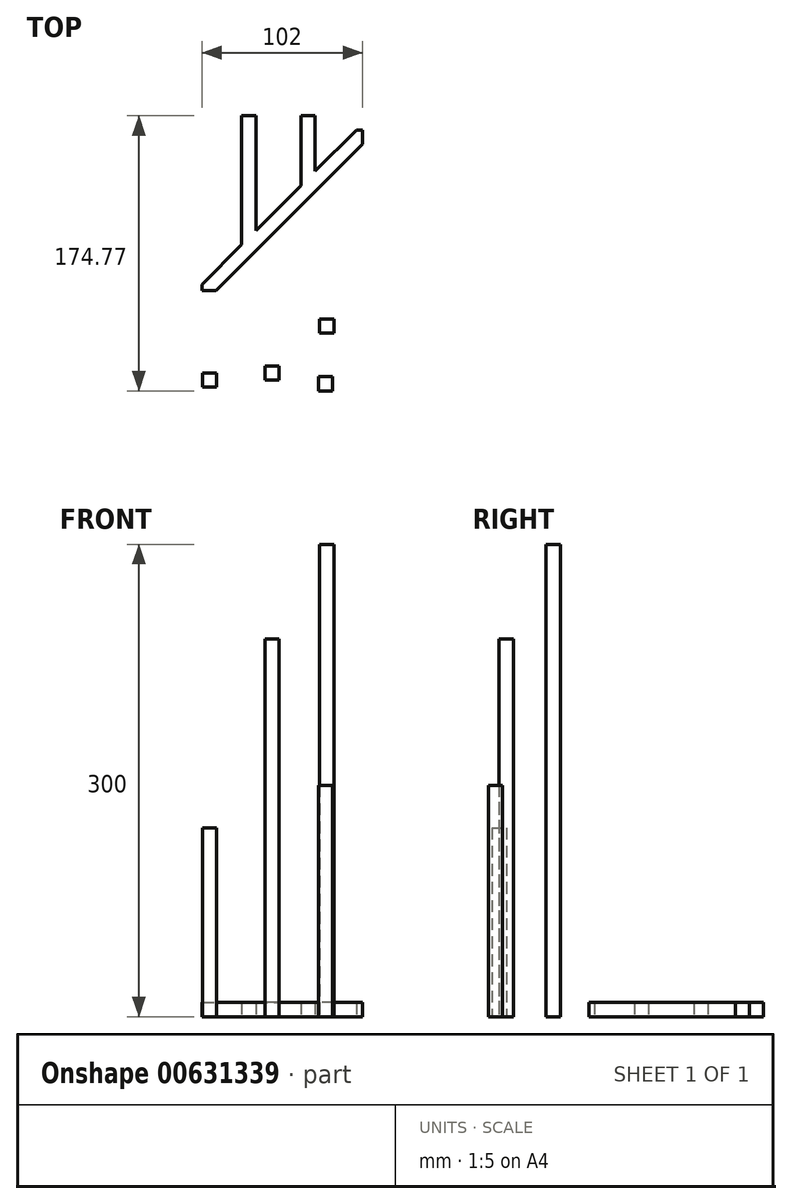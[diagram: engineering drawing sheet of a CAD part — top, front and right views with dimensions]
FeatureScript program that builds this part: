
annotation { "Feature Type Name" : "Feature", "Feature Type Description" : "" }
export const myFeature = defineFeature(function(context is Context, id is Id, definition is map)
    precondition{}
    {
        {
            var Q0;
            Q0=qCreatedBy(makeId("Top.planeOp"),FACE);
            var sketch = newSketch(context, id + "F0", { "sketchPlane" : qUnion([Q0])});
            skLineSegment(sketch, "E0.bottom", {"start": v(4.5, -4.5) * mm, "end": v(-4.5, -4.5) * mm});
            skLineSegment(sketch, "E0.top", {"start": v(4.5, 4.5) * mm, "end": v(-4.5, 4.5) * mm});
            skLineSegment(sketch, "E0.left", {"start": v(4.5, -4.5) * mm, "end": v(4.5, 4.5) * mm});
            skLineSegment(sketch, "E0.right", {"start": v(-4.5, -4.5) * mm, "end": v(-4.5, 4.5) * mm});
            skPoint(sketch, "E0.middle", {"position": v(0, 0) * mm});
            skSolve(sketch);
        }
        {
            var Q0;
            Q0=makeQuery(id+"F0.imprint","IMPRINT",FACE,{"disambiguationData":[TD([[makeQuery(id+"F0.imprint","IMPRINT",EDGE,{"derivedFrom":sQuery(id+"F0.wireOp",EDGE,"E0.bottom")}),-1.0]])]});
            extrude(context, id + "F1", {"entities" : qUnion([Q0]), "depth" : 300 * mm, "offsetDistance" : 25 * mm});
        }
        {
            var Q0;
            Q0=qCreatedBy(makeId("Top.planeOp"),FACE);
            var sketch = newSketch(context, id + "F2", { "sketchPlane" : qUnion([Q0])});
            skLineSegment(sketch, "E1.bottom", {"start": v(-69.91, -38.78) * mm, "end": v(-78.91, -38.78) * mm});
            skLineSegment(sketch, "E1.top", {"start": v(-69.91, -29.78) * mm, "end": v(-78.91, -29.78) * mm});
            skLineSegment(sketch, "E1.left", {"start": v(-69.91, -38.78) * mm, "end": v(-69.91, -29.78) * mm});
            skLineSegment(sketch, "E1.right", {"start": v(-78.91, -38.78) * mm, "end": v(-78.91, -29.78) * mm});
            skPoint(sketch, "E1.middle", {"position": v(-74.41, -34.28) * mm});
            skSolve(sketch);
        }
        {
            var Q0;
            Q0=makeQuery(id+"F2.imprint","IMPRINT",FACE,{"disambiguationData":[TD([[makeQuery(id+"F2.imprint","IMPRINT",EDGE,{"derivedFrom":sQuery(id+"F2.wireOp",EDGE,"E1.bottom")}),-1.0]])]});
            extrude(context, id + "F3", {"entities" : qUnion([Q0]), "depth" : 120 * mm, "offsetDistance" : 25 * mm});
        }
        {
            var Q0;
            Q0=qCreatedBy(makeId("Top.planeOp"),FACE);
            var sketch = newSketch(context, id + "F4", { "sketchPlane" : qUnion([Q0])});
            skLineSegment(sketch, "E2.bottom", {"start": v(-30.29, -34.37) * mm, "end": v(-39.29, -34.37) * mm});
            skLineSegment(sketch, "E2.top", {"start": v(-30.29, -25.37) * mm, "end": v(-39.29, -25.37) * mm});
            skLineSegment(sketch, "E2.left", {"start": v(-30.29, -34.37) * mm, "end": v(-30.29, -25.37) * mm});
            skLineSegment(sketch, "E2.right", {"start": v(-39.29, -34.37) * mm, "end": v(-39.29, -25.37) * mm});
            skPoint(sketch, "E2.middle", {"position": v(-34.79, -29.87) * mm});
            skSolve(sketch);
        }
        {
            var Q0;
            Q0=makeQuery(id+"F4.imprint","IMPRINT",FACE,{"disambiguationData":[TD([[makeQuery(id+"F4.imprint","IMPRINT",EDGE,{"derivedFrom":sQuery(id+"F4.wireOp",EDGE,"E2.bottom")}),-1.0]])]});
            extrude(context, id + "F5", {"entities" : qUnion([Q0]), "depth" : 240 * mm, "offsetDistance" : 25 * mm});
        }
        {
            var Q0;
            Q0=qCreatedBy(makeId("Top.planeOp"),FACE);
            var sketch = newSketch(context, id + "F6", { "sketchPlane" : qUnion([Q0])});
            skLineSegment(sketch, "E3.bottom", {"start": v(-83.02, 128.34) * mm, "end": v(22.7, 128.34) * mm});
            skLineSegment(sketch, "E3.top", {"start": v(-83.02, 22.62) * mm, "end": v(22.7, 22.62) * mm});
            skLineSegment(sketch, "E3.left", {"start": v(-83.02, 128.34) * mm, "end": v(-83.02, 22.62) * mm});
            skLineSegment(sketch, "E3.right", {"start": v(22.7, 128.34) * mm, "end": v(22.7, 22.62) * mm});
            skLineSegment(sketch, "E4", {"start": v(-83.02, 22.62) * mm, "end": v(22.7, 128.34) * mm});
            skLineSegment(sketch, "E5", {"start": v(22.7, 128.34) * mm, "end": v(22.7, 115.62) * mm});
            skLineSegment(sketch, "E6", {"start": v(22.7, 115.62) * mm, "end": v(-70.3, 22.62) * mm});
            skLineSegment(sketch, "E7", {"start": v(-79.3, 22.62) * mm, "end": v(-79.3, 26.34) * mm});
            skLineSegment(sketch, "E8", {"start": v(22.7, 124.62) * mm, "end": v(18.98, 124.62) * mm});
            skLineSegment(sketch, "E9.bottom", {"start": v(22.7, 22.62) * mm, "end": v(31.7, 22.62) * mm});
            skLineSegment(sketch, "E9.top", {"start": v(22.7, 128.34) * mm, "end": v(31.7, 128.34) * mm});
            skLineSegment(sketch, "E9.left", {"start": v(22.7, 22.62) * mm, "end": v(22.7, 128.34) * mm});
            skLineSegment(sketch, "E10.top", {"start": v(-83.02, 133.62) * mm, "end": v(22.7, 133.62) * mm});
            skLineSegment(sketch, "E10.left", {"start": v(-83.02, 128.34) * mm, "end": v(-83.02, 133.62) * mm});
            skLineSegment(sketch, "E10.right", {"start": v(22.7, 128.34) * mm, "end": v(22.7, 133.62) * mm});
            skLineSegment(sketch, "E11", {"start": v(-45.01, 60.63) * mm, "end": v(-45.01, 133.62) * mm});
            skLineSegment(sketch, "E12", {"start": v(-54.01, 51.63) * mm, "end": v(-54.01, 133.62) * mm});
            skLineSegment(sketch, "E13", {"start": v(-16.33, 89.31) * mm, "end": v(-16.33, 133.62) * mm});
            skLineSegment(sketch, "E14", {"start": v(-7.33, 98.31) * mm, "end": v(-7.33, 133.62) * mm});
            skSolve(sketch);
        }
        {
            var Q0;
            {var subQ0=sQuery(id+"F6.wireOp",EDGE,"E6");Q0=makeQuery(id+"F6.imprint","IMPRINT",FACE,{"disambiguationData":[TD([[makeQuery(id+"F6.imprint","IMPRINT",EDGE,{"derivedFrom":subQ0}),-1.0]])]});}
            var Q1;
            {var subQ0=sQuery(id+"F6.wireOp",EDGE,"GLqQGj4I-6qy6-CAvR-qAdy-Jy6QRoEFBSq3");var subQ1=sQuery(id+"F6.wireOp",EDGE,"E9.left");var subQ2=makeQuery(id+"F6.imprint","INTERSECT",VERTEX,{"derivedFrom":[subQ1,subQ0]});Q1=makeQuery(id+"F6.imprint","IMPRINT",FACE,{"disambiguationData":[TD([[makeQuery(id+"F6.imprint","IMPRINT",EDGE,{"disambiguationData":[TD([[subQ2,-1.0]])],"derivedFrom":subQ1}),-1.0]])]});}
            var Q2;
            {var subQ0=sQuery(id+"F6.wireOp",EDGE,"KDLGF8DV-3HPa-q44J-DO2s-JYTbupPruN74");var subQ1=sQuery(id+"F6.wireOp",EDGE,"E9.left");var subQ2=makeQuery(id+"F6.imprint","INTERSECT",VERTEX,{"derivedFrom":[subQ1,subQ0]});Q2=makeQuery(id+"F6.imprint","IMPRINT",FACE,{"disambiguationData":[TD([[makeQuery(id+"F6.imprint","IMPRINT",EDGE,{"disambiguationData":[TD([[subQ2,-1.0]])],"derivedFrom":subQ1}),-1.0]])]});}
            var Q3;
            {var subQ0=sQuery(id+"F6.wireOp",EDGE,"E11");var subQ1=sQuery(id+"F6.wireOp",EDGE,"E4");var subQ2=makeQuery(id+"F6.imprint","INTERSECT",VERTEX,{"derivedFrom":[subQ1,subQ0]});Q3=makeQuery(id+"F6.imprint","IMPRINT",FACE,{"disambiguationData":[TD([[makeQuery(id+"F6.imprint","IMPRINT",EDGE,{"disambiguationData":[TD([[subQ2,1.0]])],"derivedFrom":subQ1}),1.0]])]});}
            var Q4;
            {var subQ0=sQuery(id+"F6.wireOp",EDGE,"E12");var subQ1=sQuery(id+"F6.wireOp",EDGE,"E3.bottom");var subQ2=makeQuery(id+"F6.imprint","INTERSECT",VERTEX,{"derivedFrom":[subQ1,subQ0]});Q4=makeQuery(id+"F6.imprint","IMPRINT",FACE,{"disambiguationData":[TD([[makeQuery(id+"F6.imprint","IMPRINT",EDGE,{"disambiguationData":[TD([[subQ2,-1.0]])],"derivedFrom":subQ1}),1.0]])]});}
            var Q5;
            {var subQ0=sQuery(id+"F6.wireOp",EDGE,"E13");var subQ1=sQuery(id+"F6.wireOp",EDGE,"E4");var subQ2=makeQuery(id+"F6.imprint","INTERSECT",VERTEX,{"derivedFrom":[subQ1,subQ0]});Q5=makeQuery(id+"F6.imprint","IMPRINT",FACE,{"disambiguationData":[TD([[makeQuery(id+"F6.imprint","IMPRINT",EDGE,{"disambiguationData":[TD([[subQ2,-1.0]])],"derivedFrom":subQ1}),1.0]])]});}
            var Q6;
            {var subQ0=sQuery(id+"F6.wireOp",EDGE,"E13");var subQ1=sQuery(id+"F6.wireOp",EDGE,"E3.bottom");var subQ2=makeQuery(id+"F6.imprint","INTERSECT",VERTEX,{"derivedFrom":[subQ1,subQ0]});Q6=makeQuery(id+"F6.imprint","IMPRINT",FACE,{"disambiguationData":[TD([[makeQuery(id+"F6.imprint","IMPRINT",EDGE,{"disambiguationData":[TD([[subQ2,-1.0]])],"derivedFrom":subQ1}),1.0]])]});}
            extrude(context, id + "F7", {"entities" : qUnion([Q0, Q1, Q2, Q3, Q4, Q5, Q6]), "depth" : 9 * mm, "offsetDistance" : 25 * mm});
        }
        {
            var Q0;
            Q0=qCreatedBy(makeId("Top.planeOp"),FACE);
            var sketch = newSketch(context, id + "F8", { "sketchPlane" : qUnion([Q0])});
            skLineSegment(sketch, "E15.bottom", {"start": v(3.67, -41.15) * mm, "end": v(-5.33, -41.15) * mm});
            skLineSegment(sketch, "E15.top", {"start": v(3.67, -32.15) * mm, "end": v(-5.33, -32.15) * mm});
            skLineSegment(sketch, "E15.left", {"start": v(3.67, -41.15) * mm, "end": v(3.67, -32.15) * mm});
            skLineSegment(sketch, "E15.right", {"start": v(-5.33, -41.15) * mm, "end": v(-5.33, -32.15) * mm});
            skPoint(sketch, "E15.middle", {"position": v(-0.83, -36.65) * mm});
            skSolve(sketch);
        }
        {
            var Q0;
            Q0=makeQuery(id+"F8.imprint","IMPRINT",FACE,{"disambiguationData":[TD([[makeQuery(id+"F8.imprint","IMPRINT",EDGE,{"derivedFrom":sQuery(id+"F8.wireOp",EDGE,"E15.bottom")}),-1.0]])]});
            extrude(context, id + "F9", {"entities" : qUnion([Q0]), "depth" : 147 * mm, "offsetDistance" : 25 * mm});
        }
    });
